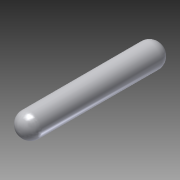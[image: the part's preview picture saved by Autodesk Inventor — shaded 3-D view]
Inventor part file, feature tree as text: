
AUTODESK INVENTOR PART (.ipt)
format: ipt  version: 2013 (Build 170138000, 138)  size: 91,648 bytes
history: native  units: in
note: dims shown in document units (in); Inventor stores cm internally (conversion verified against a paired STEP export)
features: fillet x2, extrude x1, sketch x1
ambient origin geometry x8: Origin, YZ Plane, XZ Plane, XY Plane, X Axis, Y Axis, Z Axis, Center Point
bodies: Solid1 (feature_tree)
feature tree (4):
  extrude  "Extrusion1"  Depth=12.0in TaperAngle=0.0deg
  fillet  "Fillet1"  Radius=0.95in
  fillet  "Fillet2"  Radius=0.95in
  sketch  "Sketch1"  dims[d0=2.0in d3=12.0in d4=0.0in d5=0.95in d6=0.95in]
